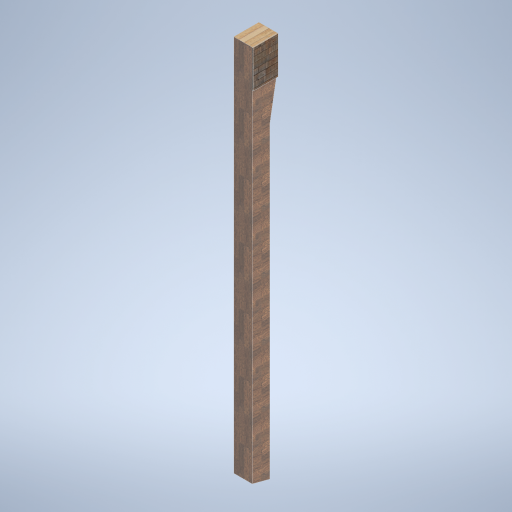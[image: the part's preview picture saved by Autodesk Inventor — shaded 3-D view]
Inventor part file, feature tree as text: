
AUTODESK INVENTOR PART (.ipt)
format: ipt  version: 2024.2 (Build 282272000, 272)  size: 337,920 bytes
history: native  units: mm
features: extrude x2, sketch x2
ambient origin geometry x8: Origin, YZ Plane, XZ Plane, XY Plane, X Axis, Y Axis, Z Axis, Center Point
bodies: Solid1 (feature_tree)
feature tree (4):
  extrude  "Extrusion1"  Depth=40000.000002mm
  extrude  "Extrusion2"  Depth=10.0mm
  sketch  "Sketch2"  dims[d0=40000.000002mm d1=300.0mm]
  sketch  "Sketch3"  dims[d2=200.0mm d3=0.0mm d5=400.0mm d6=1.745329mm d7=1.745329mm d8=10.0mm d9=10.0mm d10=10.0mm d11=0.0mm d12=500.0mm d13=0.872665mm d14=500.0mm d15=0.872665mm]
